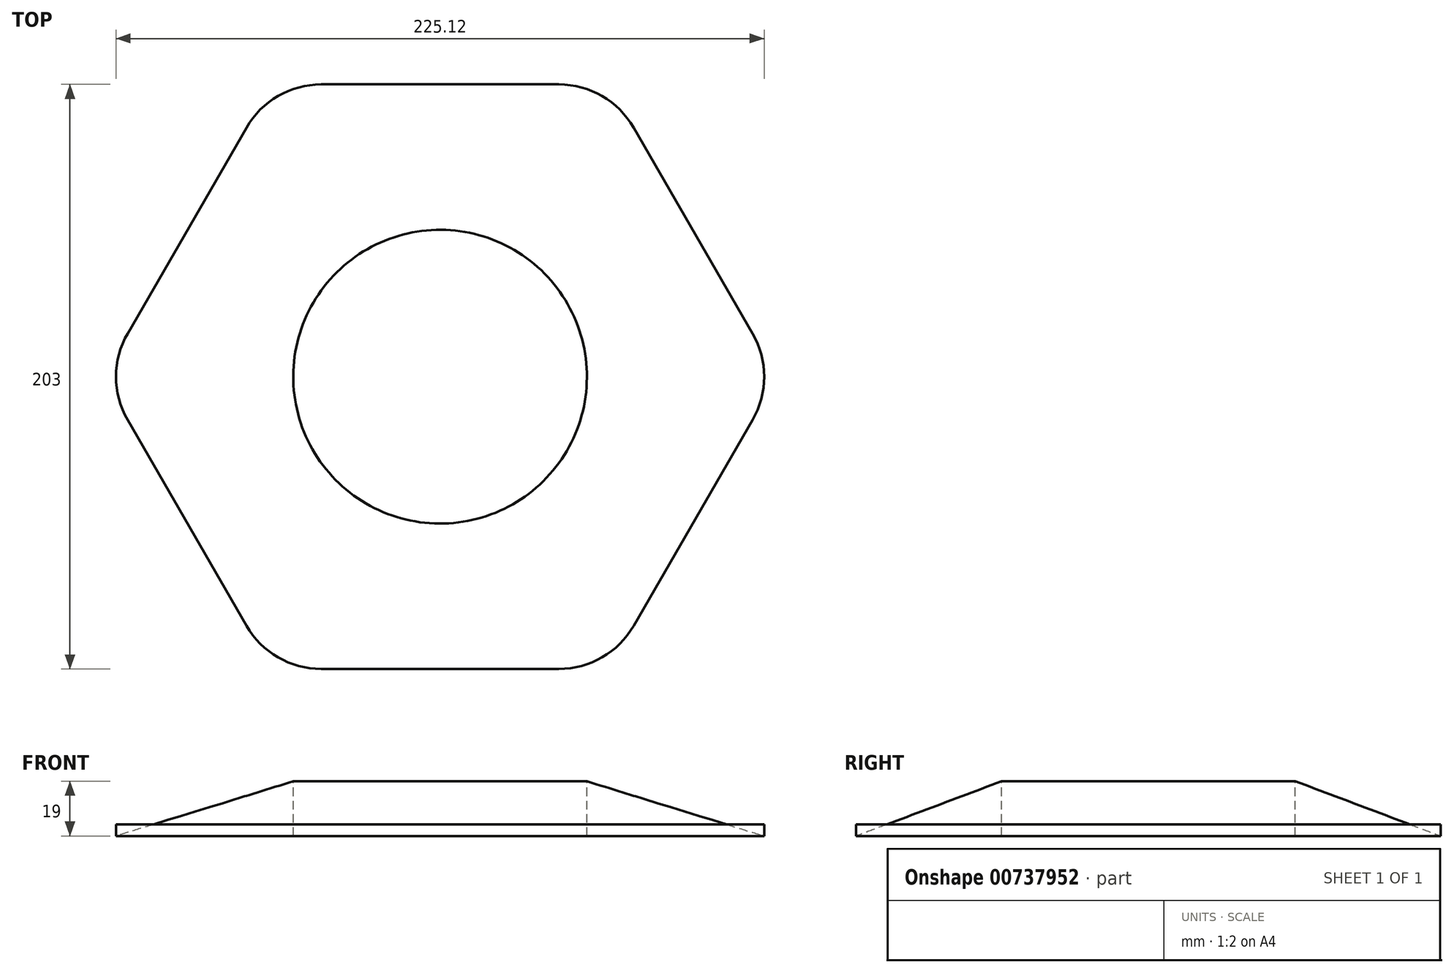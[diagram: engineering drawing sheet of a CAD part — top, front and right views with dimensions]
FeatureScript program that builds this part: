
annotation { "Feature Type Name" : "Feature", "Feature Type Description" : "" }
export const myFeature = defineFeature(function(context is Context, id is Id, definition is map)
    precondition{}
    {
        {
            var Q0;
            Q0=qCreatedBy(makeId("Top.planeOp"),FACE);
            var sketch = newSketch(context, id + "F0", { "sketchPlane" : qUnion([Q0])});
            skLineSegment(sketch, "E0.0", {"start": v(-41.28, 101.5) * mm, "end": v(41.28, 101.5) * mm});
            skLineSegment(sketch, "E0.1", {"start": v(67.26, 86.5) * mm, "end": v(108.54, 15) * mm});
            skLineSegment(sketch, "E0.2", {"start": v(108.54, -15) * mm, "end": v(67.26, -86.5) * mm});
            skLineSegment(sketch, "E0.3", {"start": v(41.28, -101.5) * mm, "end": v(-41.28, -101.5) * mm});
            skLineSegment(sketch, "E0.4", {"start": v(-67.26, -86.5) * mm, "end": v(-108.54, -15) * mm});
            skLineSegment(sketch, "E0.5", {"start": v(-108.54, 15) * mm, "end": v(-67.26, 86.5) * mm});
            skPoint(sketch, "E1.visualSharp", {"position": v(-58.6, 101.5) * mm});
            skArc(sketch, "E1.filletArc", {"start": v(-41.28, 101.5) * mm, "mid": v(-56.28, 97.48) * mm, "end": v(-67.26, 86.5) * mm});
            skPoint(sketch, "E2.visualSharp", {"position": v(58.6, 101.5) * mm});
            skArc(sketch, "E2.filletArc", {"start": v(67.26, 86.5) * mm, "mid": v(56.28, 97.48) * mm, "end": v(41.28, 101.5) * mm});
            skPoint(sketch, "E3.visualSharp", {"position": v(117.2, 0) * mm});
            skArc(sketch, "E3.filletArc", {"start": v(108.54, -15) * mm, "mid": v(112.56, 0) * mm, "end": v(108.54, 15) * mm});
            skPoint(sketch, "E4.visualSharp", {"position": v(58.6, -101.5) * mm});
            skArc(sketch, "E4.filletArc", {"start": v(41.28, -101.5) * mm, "mid": v(56.28, -97.48) * mm, "end": v(67.26, -86.5) * mm});
            skPoint(sketch, "E5.visualSharp", {"position": v(-58.6, -101.5) * mm});
            skArc(sketch, "E5.filletArc", {"start": v(-67.26, -86.5) * mm, "mid": v(-56.28, -97.48) * mm, "end": v(-41.28, -101.5) * mm});
            skPoint(sketch, "E6.visualSharp", {"position": v(-117.2, 0) * mm});
            skArc(sketch, "E6.filletArc", {"start": v(-108.54, 15) * mm, "mid": v(-112.56, 0) * mm, "end": v(-108.54, -15) * mm});
            skPoint(sketch, "E7", {"position": v(-31.2, 53.32) * mm});
            skSolve(sketch);
        }
        {
            var Q0;
            Q0=qCreatedBy(makeId("Top.planeOp"),FACE);
            cPlane(context, id + "F1", {"entities" : qUnion([Q0]), "cplaneType" : CPlaneType.OFFSET, "offset" : 19 * mm, "width" : 150 * mm, "height" : 150 * mm});
        }
        {
            var Q0;
            Q0=qCreatedBy(id+"F1.planeOp",FACE);
            var sketch = newSketch(context, id + "F2", { "sketchPlane" : qUnion([Q0])});
            skCircle(sketch, "E8", {"center": v(0, 0) * mm, "radius": 51 * mm});
            skLineSegment(sketch, "E9", {"start": v(0, 0) * mm, "end": v(-37.85, 168) * mm, "construction": true});
            skLineSegment(sketch, "E10", {"start": v(-37.85, 168) * mm, "end": v(39.82, -176.73) * mm, "construction": true});
            skPoint(sketch, "E11", {"position": v(-18.8, 83.48) * mm});
            skPoint(sketch, "E12", {"position": v(-19.35, 47.19) * mm});
            skPoint(sketch, "E13", {"position": v(-2.76, 50.93) * mm});
            skLineSegment(sketch, "E14", {"start": v(-19.35, 47.19) * mm, "end": v(-28.05, 62.47) * mm});
            skLineSegment(sketch, "E15", {"start": v(-28.05, 62.47) * mm, "end": v(-14.99, 69.9) * mm});
            skSolve(sketch);
        }
        {
            var Q0;
            Q0=makeQuery(id+"F2.imprint","IMPRINT",FACE,{"disambiguationData":[TD([[makeQuery(id+"F2.imprint","IMPRINT",EDGE,{"derivedFrom":sQuery(id+"F2.wireOp",EDGE,"E8")}),1.0]])]});
            var Q1;
            Q1=makeQuery(id+"F0.imprint","IMPRINT",FACE,{"disambiguationData":[TD([[makeQuery(id+"F0.imprint","IMPRINT",EDGE,{"derivedFrom":sQuery(id+"F0.wireOp",EDGE,"E0.0")}),-1.0]])]});
            loft(context, id + "F3", {"sheetProfilesArray" : [{ "sheetProfileEntities" : qUnion([Q0]) }, { "sheetProfileEntities" : qUnion([Q1]) }]});
        }
        {
            var Q0;
            Q0=makeQuery(id+"F3.opLoft","CAP_FACE",FACE,{"disambiguationData":[OSD([makeQuery(id+"F2.imprint","IMPRINT",FACE,{"disambiguationData":[TD([[makeQuery(id+"F2.imprint","IMPRINT",EDGE,{"derivedFrom":sQuery(id+"F2.wireOp",EDGE,"E8")}),1.0]])]})])],"isStart":true});
            var Q1;
            Q1 = qConstructionFilter(qBodyType(qCreatedBy(id + "F2" ,EDGE), BodyType.WIRE), ConstructionObject.NO);
            extrude(context, id + "F4", {"entities" : qUnion([Q0]), "operationType" : NewBodyOperationType.REMOVE, "surfaceEntities" : qUnion([Q1]), "endBound" : BoundingType.THROUGH_ALL, "oppositeDirection" : true, "depth" : 25 * mm, "offsetDistance" : 25 * mm});
        }
        {
            var Q0;
            Q0 = qSketchRegion(id + "F0", true);
            extrude(context, id + "F5", {"entities" : qUnion([Q0]), "depth" : 4 * mm, "offsetDistance" : 25 * mm});
        }
    });
